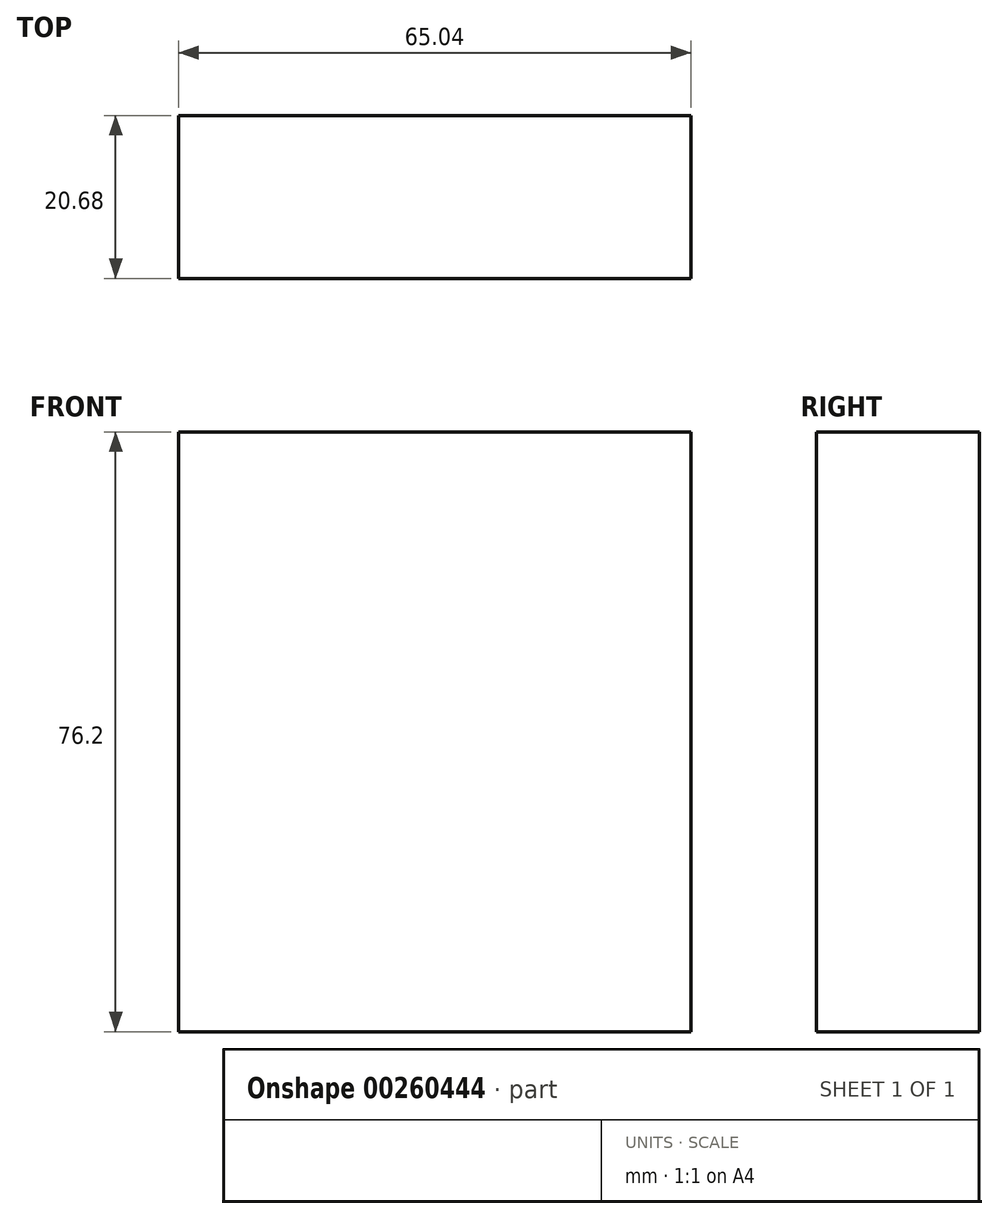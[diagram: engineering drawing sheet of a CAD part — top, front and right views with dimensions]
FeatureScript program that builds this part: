
annotation { "Feature Type Name" : "Feature", "Feature Type Description" : "" }
export const myFeature = defineFeature(function(context is Context, id is Id, definition is map)
    precondition{}
    {
        {
            var Q0;
            Q0=qCreatedBy(makeId("Top.planeOp"),FACE);
            var sketch = newSketch(context, id + "F0", { "sketchPlane" : qUnion([Q0])});
            skLineSegment(sketch, "E0.bottom", {"start": v(-32.52, 10.34) * mm, "end": v(32.52, 10.34) * mm});
            skLineSegment(sketch, "E0.top", {"start": v(-32.52, -10.34) * mm, "end": v(32.52, -10.34) * mm});
            skLineSegment(sketch, "E0.left", {"start": v(-32.52, 10.34) * mm, "end": v(-32.52, -10.34) * mm});
            skLineSegment(sketch, "E0.right", {"start": v(32.52, 10.34) * mm, "end": v(32.52, -10.34) * mm});
            skPoint(sketch, "E0.middle", {"position": v(0, 0) * mm});
            skSolve(sketch);
        }
        {
            var Q0;
            Q0 = qSketchRegion(id + "F0", true);
            extrude(context, id + "F1", {"entities" : qUnion([Q0]), "depth" : 76.2 * mm});
        }
    });
